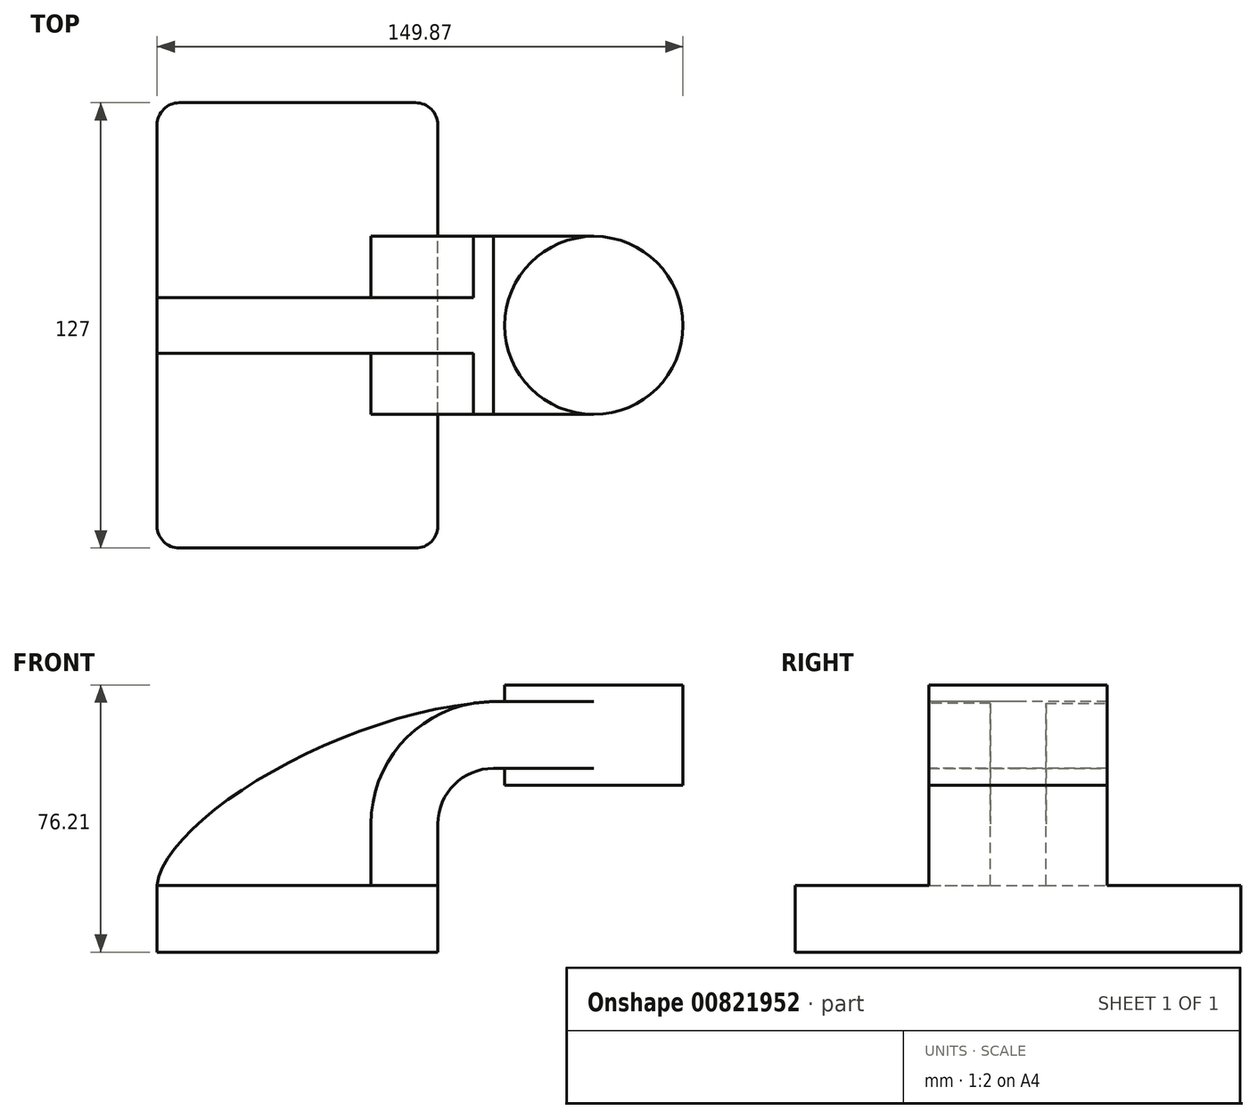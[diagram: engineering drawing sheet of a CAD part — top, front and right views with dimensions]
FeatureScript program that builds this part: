
annotation { "Feature Type Name" : "Feature", "Feature Type Description" : "" }
export const myFeature = defineFeature(function(context is Context, id is Id, definition is map)
    precondition{}
    {
        {
            var Q0;
            Q0=qCreatedBy(makeId("Front.planeOp"),FACE);
            var sketch = newSketch(context, id + "F0", { "sketchPlane" : qUnion([Q0])});
            skLineSegment(sketch, "E0.bottom", {"start": v(40, 9.53) * mm, "end": v(-40, 9.53) * mm});
            skLineSegment(sketch, "E0.top", {"start": v(40, -9.52) * mm, "end": v(-40, -9.52) * mm});
            skLineSegment(sketch, "E0.left", {"start": v(40, 9.53) * mm, "end": v(40, -9.52) * mm});
            skLineSegment(sketch, "E0.right", {"start": v(-40, 9.53) * mm, "end": v(-40, -9.52) * mm});
            skPoint(sketch, "E0.middle", {"position": v(0, 0) * mm});
            skLineSegment(sketch, "E1.bottom", {"start": v(109.85, 38.1) * mm, "end": v(59.05, 38.1) * mm});
            skLineSegment(sketch, "E1.top", {"start": v(109.85, 66.68) * mm, "end": v(59.05, 66.68) * mm});
            skLineSegment(sketch, "E1.left", {"start": v(109.85, 38.1) * mm, "end": v(109.85, 66.68) * mm});
            skLineSegment(sketch, "E1.right", {"start": v(59.05, 38.1) * mm, "end": v(59.05, 66.68) * mm});
            skPoint(sketch, "E1.middle", {"position": v(84.45, 52.39) * mm});
            skLineSegment(sketch, "E2", {"start": v(40, 9.53) * mm, "end": v(40, 27) * mm});
            skLineSegment(sketch, "E3", {"start": v(55.88, 42.88) * mm, "end": v(84.45, 42.88) * mm});
            skArc(sketch, "E4", {"start": v(40, 27) * mm, "mid": v(44.65, 38.23) * mm, "end": v(55.88, 42.88) * mm});
            skLineSegment(sketch, "E5.0", {"start": v(55.88, 61.93) * mm, "end": v(84.45, 61.93) * mm});
            skArc(sketch, "E5.1", {"start": v(20.96, 27) * mm, "mid": v(31.18, 51.7) * mm, "end": v(55.88, 61.93) * mm});
            skLineSegment(sketch, "E5.2", {"start": v(20.96, 9.53) * mm, "end": v(20.96, 27) * mm});
            skLineSegment(sketch, "E6", {"start": v(84.45, 38.1) * mm, "end": v(84.45, 66.68) * mm});
            skFitSpline(sketch, "E7", {"points": [v(-40, 9.52) * mm, v(55.88, 61.93) * mm], "startDerivative": vector(6.66, 58.2) * mm, "endDerivative": vector(124.68, 6.69) * mm});
            skSolve(sketch);
        }
        {
            var Q0;
            Q0=makeQuery(id+"F0.imprint","IMPRINT",FACE,{"disambiguationData":[TD([[makeQuery(id+"F0.imprint","IMPRINT",EDGE,{"derivedFrom":sQuery(id+"F0.wireOp",EDGE,"E0.top")}),-1.0]])]});
            extrude(context, id + "F1", {"entities" : qUnion([Q0]), "endBound" : BoundingType.SYMMETRIC, "depth" : 127 * mm, "offsetDistance" : 25.4 * mm});
        }
        {
            var Q0;
            {var subQ4=sQuery(id+"F0.wireOp",EDGE,"E2");Q0=makeQuery(id+"F0.imprint","IMPRINT",FACE,{"disambiguationData":[TD([[makeQuery(id+"F0.imprint","IMPRINT",EDGE,{"derivedFrom":subQ4}),1.0]])]});}
            var Q1;
            {var subQ0=sQuery(id+"F0.wireOp",EDGE,"E3");var subQ1=sQuery(id+"F0.wireOp",EDGE,"E1.right");var subQ2=makeQuery(id+"F0.imprint","INTERSECT",VERTEX,{"derivedFrom":[subQ1,subQ0]});Q1=makeQuery(id+"F0.imprint","IMPRINT",FACE,{"disambiguationData":[TD([[makeQuery(id+"F0.imprint","IMPRINT",EDGE,{"disambiguationData":[TD([[subQ2,-1.0]])],"derivedFrom":subQ1}),-1.0]])]});}
            extrude(context, id + "F2", {"entities" : qUnion([Q0, Q1]), "operationType" : NewBodyOperationType.ADD, "endBound" : BoundingType.SYMMETRIC, "depth" : 50.8 * mm, "offsetDistance" : 25.4 * mm});
        }
        {
            var Q0;
            {var subQ3=sQuery(id+"F0.wireOp",EDGE,"E5.2");Q0=makeQuery(id+"F0.imprint","IMPRINT",FACE,{"disambiguationData":[TD([[makeQuery(id+"F0.imprint","IMPRINT",EDGE,{"derivedFrom":subQ3}),1.0]])]});}
            extrude(context, id + "F3", {"entities" : qUnion([Q0]), "operationType" : NewBodyOperationType.ADD, "endBound" : BoundingType.SYMMETRIC, "depth" : 15.88 * mm, "offsetDistance" : 25.4 * mm});
        }
        {
            var Q0;
            {var subQ0=sQuery(id+"F0.wireOp",EDGE,"E1.left");Q0=makeQuery(id+"F0.imprint","IMPRINT",FACE,{"disambiguationData":[TD([[makeQuery(id+"F0.imprint","IMPRINT",EDGE,{"derivedFrom":subQ0}),1.0]])]});}
            var Q1;
            Q1=sQuery(id+"F0.wireOp",EDGE,"E6");
            revolve(context, id + "F4", {"operationType" : NewBodyOperationType.ADD, "surfaceOperationType" : NewSurfaceOperationType.NEW, "entities" : qUnion([Q0]), "axis" : qUnion([Q1]), "revolveType" : RevolveType.FULL});
        }
        {
            var Q0;
            Q0=makeQuery(id+"F1.opExtrude","CAP_EDGE",EDGE,{"disambiguationData":[OSD([sQuery(id+"F0.wireOp",EDGE,"E0.right")])],"isStart":false});
            var Q1;
            Q1=makeQuery(id+"F1.opExtrude","CAP_EDGE",EDGE,{"disambiguationData":[OSD([sQuery(id+"F0.wireOp",EDGE,"E0.left")])],"isStart":false});
            var Q2;
            Q2=makeQuery(id+"F1.opExtrude","CAP_EDGE",EDGE,{"disambiguationData":[OSD([sQuery(id+"F0.wireOp",EDGE,"E0.left")])],"isStart":true});
            var Q3;
            Q3=makeQuery(id+"F1.opExtrude","CAP_EDGE",EDGE,{"disambiguationData":[OSD([sQuery(id+"F0.wireOp",EDGE,"E0.right")])],"isStart":true});
            fillet(context, id + "F5", {"entities" : qUnion([Q0, Q1, Q2, Q3]), "radius" : 6.35 * mm, "tangentPropagation" : true, "allowEdgeOverflow" : false});
        }
    });
